# Revit family: 15224 Умная урна Смартчейн версия 1.0 Хоббика
name_source: partatom
category: Антураж
revit_build: Autodesk Revit 2018 (Build: 20180423_1000(x64)
units: mm (PartAtom-declared; Revit-internal decimal feet)

## family parameters
Всегда вертикально = Да
Источник визуального образа = Геометрия семейства
На основе рабочей плоскости = Нет
Общий = Нет
При загрузке вырезать с полостями = Нет
Точка расчета площади = Нет

## types (4) — shared parameters
3 секции = Нет
URL = https://hobbyka.ru
Артикул товара = Арт. 15224
Высота = 800 мм
Группа модели = Умная городская мебель
Изготовитель = ООО «Хоббика»
Материал изделия = Сталь
Цвет каркаса = Сталь
Ширина = 540 мм
Экран = Экран

## per-type parameters (varying)
| type | 1 секция | 2 секции | 4 секции | Длина | Изображение типоразмера | Описание |
| 1 секция | Да | Нет | Нет | 540 мм | Умная урна Смартчейн версия 1.0 Арт 15224 1 секция.jpeg | Умная урна Смартчейн версия 1.0. Версия на 1 секцию |
| 2 секции | Нет | Да | Нет | 1040 мм | Умная урна Смартчейн версия 1.0 Арт 15224 2 секции.jpeg | Умная урна Смартчейн версия 1.0. Версия на 2 секции |
| 3 секции | Нет | Нет | Да | 2040 мм | Умная урна Смартчейн версия 1.0 Арт 15224 3 секции.jpg | Умная урна Смартчейн версия 1.0. Версия на 4 секции |
| 4 секции | Нет | Нет | Да | 2040 мм | Умная урна Смартчейн версия 1.0 Арт 15224 4 секции.jpg | Умная урна Смартчейн версия 1.0. Версия на 4 секции |
